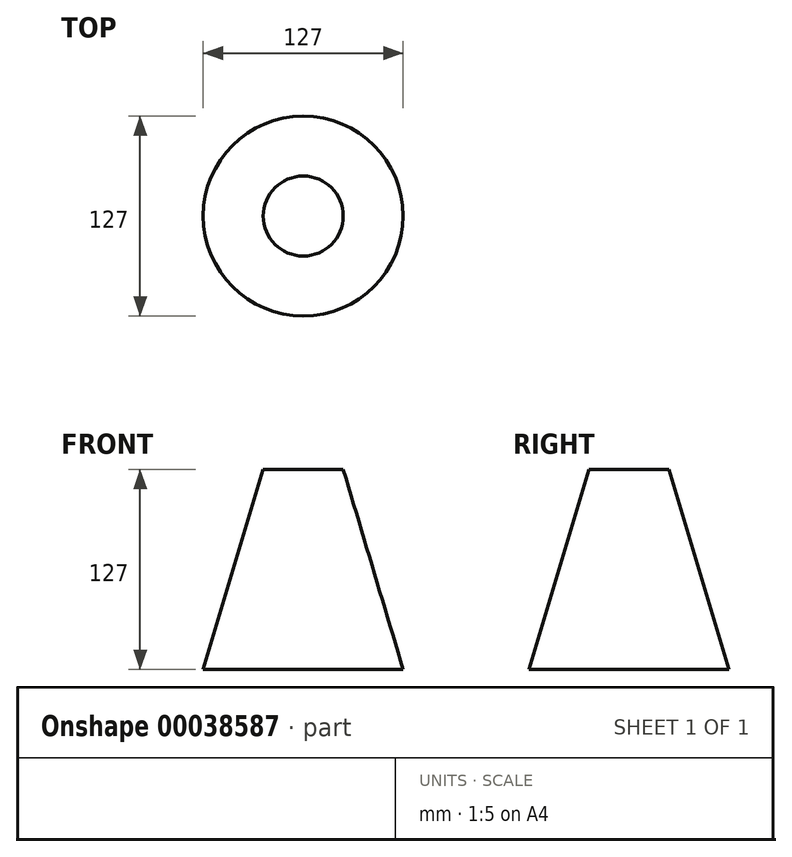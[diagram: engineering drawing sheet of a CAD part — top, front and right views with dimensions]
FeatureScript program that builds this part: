
annotation { "Feature Type Name" : "Feature", "Feature Type Description" : "" }
export const myFeature = defineFeature(function(context is Context, id is Id, definition is map)
    precondition{}
    {
        {
            var Q0;
            Q0=qCreatedBy(makeId("Top.planeOp"),FACE);
            var sketch = newSketch(context, id + "F0", { "sketchPlane" : qUnion([Q0])});
            skCircle(sketch, "E0", {"center": v(0, 0) * mm, "radius": 63.5 * mm});
            skSolve(sketch);
        }
        {
            var Q0;
            Q0=qCreatedBy(makeId("Top.planeOp"),FACE);
            cPlane(context, id + "F1", {"entities" : qUnion([Q0]), "cplaneType" : CPlaneType.OFFSET, "offset" : 127 * mm, "width" : 152.4 * mm, "height" : 152.4 * mm});
        }
        {
            var Q0;
            Q0=qCreatedBy(id+"F1.planeOp",FACE);
            var sketch = newSketch(context, id + "F2", { "sketchPlane" : qUnion([Q0])});
            skCircle(sketch, "E1", {"center": v(0, 0) * mm, "radius": 25.4 * mm});
            skSolve(sketch);
        }
        {
            var Q0;
            Q0=makeQuery(id+"F0.imprint","IMPRINT",FACE,{"disambiguationData":[TD([[makeQuery(id+"F0.imprint","IMPRINT",EDGE,{"derivedFrom":sQuery(id+"F0.wireOp",EDGE,"E0")}),1.0]])]});
            var Q1;
            Q1=makeQuery(id+"F2.imprint","IMPRINT",FACE,{"disambiguationData":[TD([[makeQuery(id+"F2.imprint","IMPRINT",EDGE,{"derivedFrom":sQuery(id+"F2.wireOp",EDGE,"E1")}),1.0]])]});
            loft(context, id + "F3", {"sheetProfilesArray" : [{ "sheetProfileEntities" : qUnion([Q0]) }, { "sheetProfileEntities" : qUnion([Q1]) }]});
        }
    });
